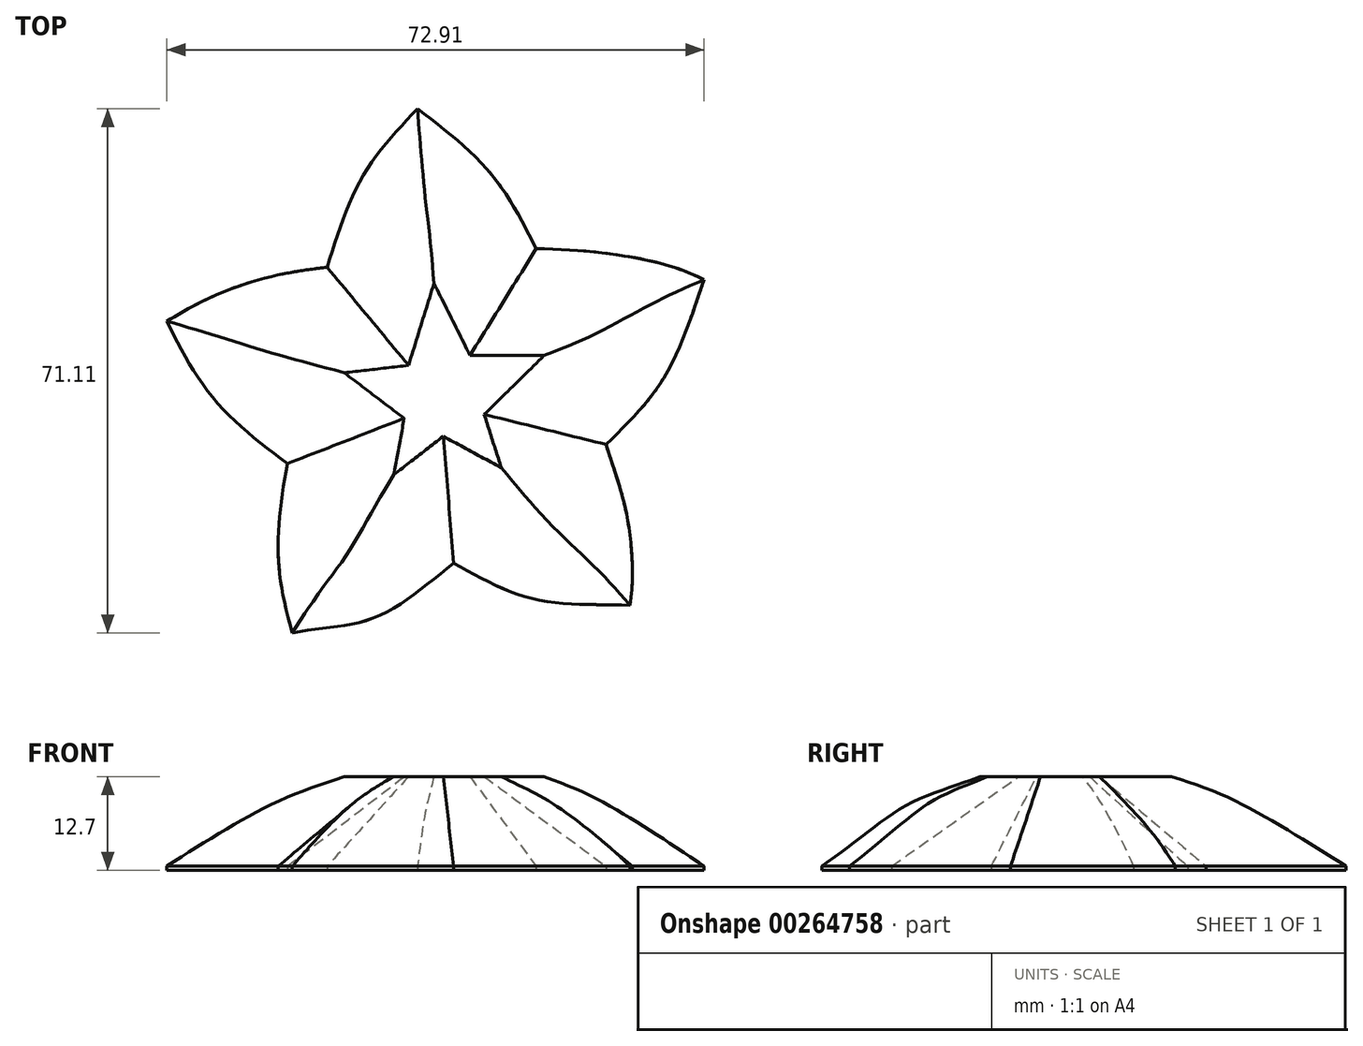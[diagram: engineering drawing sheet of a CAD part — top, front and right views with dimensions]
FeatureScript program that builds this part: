
annotation { "Feature Type Name" : "Feature", "Feature Type Description" : "" }
export const myFeature = defineFeature(function(context is Context, id is Id, definition is map)
    precondition{}
    {
        {
            var Q0;
            Q0=qCreatedBy(makeId("Top.planeOp"),FACE);
            var sketch = newSketch(context, id + "F0", { "sketchPlane" : qUnion([Q0])});
            skFitSpline(sketch, "E0", {"points": [v(-15.74, 16.87) * mm, v(-10.91, 29.2) * mm, v(-3.48, 38.37) * mm], "startDerivative": vector(7.83, 25.3) * mm, "endDerivative": vector(16.73, 17.67) * mm});
            skFitSpline(sketch, "E1", {"points": [v(-3.48, 38.37) * mm, v(6.53, 29.5) * mm, v(12.61, 19.38) * mm], "startDerivative": vector(21.09, -16.01) * mm, "endDerivative": vector(10.89, -21.77) * mm});
            skFitSpline(sketch, "E2", {"points": [v(-20.47, -32.74) * mm, v(-22.4, -21.5) * mm, v(-21.15, -9.77) * mm], "startDerivative": vector(-7.18, 25.48) * mm, "endDerivative": vector(4.42, 23.93) * mm});
            skFitSpline(sketch, "E3", {"points": [v(-37.49, 9.54) * mm, v(-25.95, 14.89) * mm, v(-15.74, 16.87) * mm], "startDerivative": vector(22.26, 14.34) * mm, "endDerivative": vector(24.18, 2.79) * mm});
            skFitSpline(sketch, "E4", {"points": [v(25.37, -29) * mm, v(12.21, -28.1) * mm, v(1.43, -23.3) * mm], "startDerivative": vector(-26.46, 1.02) * mm, "endDerivative": vector(-21.4, 11.58) * mm});
            skFitSpline(sketch, "E5", {"points": [v(35.42, 15.17) * mm, v(29.86, 1.72) * mm, v(22.1, -7.17) * mm], "startDerivative": vector(-8.74, -25) * mm, "endDerivative": vector(-17.36, -17.06) * mm});
            skFitSpline(sketch, "E6", {"points": [v(1.43, -23.3) * mm, v(-9.44, -30.72) * mm, v(-20.47, -32.74) * mm], "startDerivative": vector(-20.92, -16.22) * mm, "endDerivative": vector(-23.84, -4.88) * mm});
            skFitSpline(sketch, "E7", {"points": [v(12.61, 19.38) * mm, v(25.85, 18.19) * mm, v(35.42, 15.17) * mm], "startDerivative": vector(26.48, -0.06) * mm, "endDerivative": vector(21.8, -10.8) * mm});
            skFitSpline(sketch, "E8", {"points": [v(-21.15, -9.77) * mm, v(-31.09, -1.02) * mm, v(-37.49, 9.54) * mm], "startDerivative": vector(-21.09, 16.01) * mm, "endDerivative": vector(-10.89, 21.77) * mm});
            skFitSpline(sketch, "E9", {"points": [v(22.1, -7.17) * mm, v(24.83, -16.36) * mm, v(25.37, -29) * mm], "startDerivative": vector(8.09, -25.21) * mm, "endDerivative": vector(-3.57, -24.07) * mm});
            skSolve(sketch);
        }
        {
            var Q0;
            Q0 = qSketchRegion(id + "F0", true);
            extrude(context, id + "F1", {"entities" : qUnion([Q0]), "depth" : 12.7 * mm});
        }
        {
            var Q0;
            Q0=makeQuery(id+"F1.opExtrude","CAP_FACE",FACE,{"disambiguationData":[OSD([sQuery(id+"F0.wireOp",EDGE,"E0"),sQuery(id+"F0.wireOp",EDGE,"E1"),sQuery(id+"F0.wireOp",EDGE,"E2"),sQuery(id+"F0.wireOp",EDGE,"E3"),sQuery(id+"F0.wireOp",EDGE,"E4"),sQuery(id+"F0.wireOp",EDGE,"E5"),sQuery(id+"F0.wireOp",EDGE,"E6"),sQuery(id+"F0.wireOp",EDGE,"E7"),sQuery(id+"F0.wireOp",EDGE,"E8"),sQuery(id+"F0.wireOp",EDGE,"E9")])],"isStart":false});
            chamfer(context, id + "F2", {"entities" : qUnion([Q0]), "chamferType" : ChamferType.OFFSET_ANGLE, "width" : 14.5 * mm, "oppositeDirection" : true, "angle" : 40 * degree, "tangentPropagation" : true});
        }
    });
